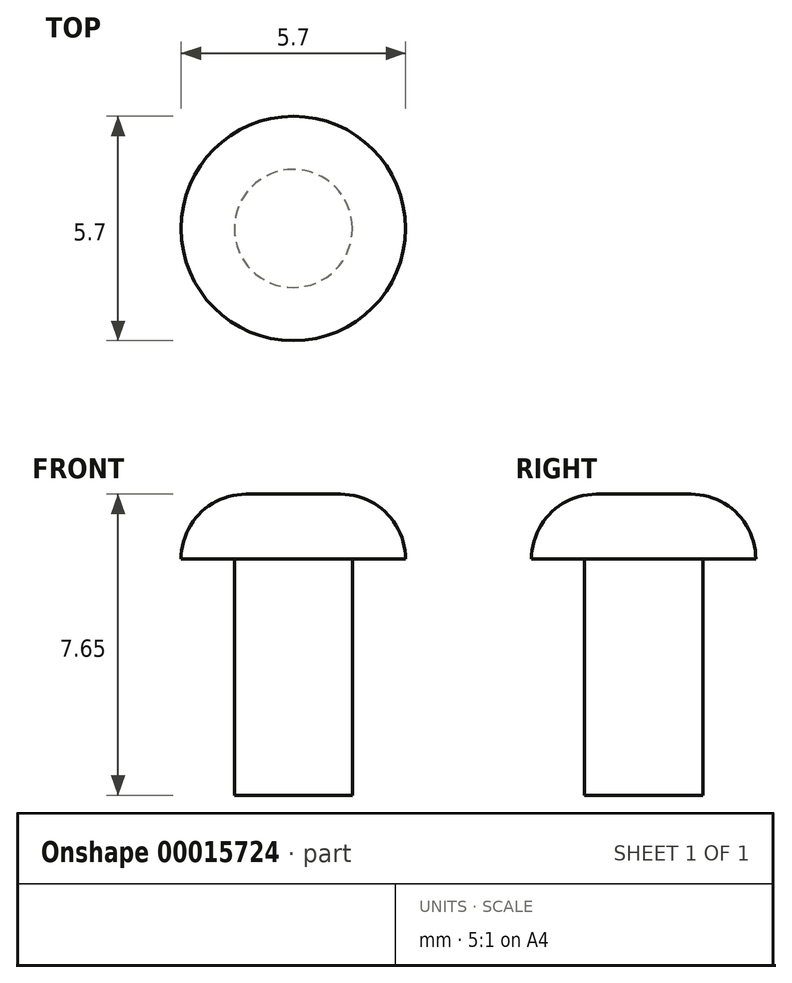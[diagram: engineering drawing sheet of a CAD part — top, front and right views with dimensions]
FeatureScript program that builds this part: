
annotation { "Feature Type Name" : "Feature", "Feature Type Description" : "" }
export const myFeature = defineFeature(function(context is Context, id is Id, definition is map)
    precondition{}
    {
        {
            var Q0;
            Q0=qCreatedBy(makeId("Top.planeOp"),FACE);
            var sketch = newSketch(context, id + "F0", { "sketchPlane" : qUnion([Q0])});
            skCircle(sketch, "E0", {"center": v(0, 0) * mm, "radius": 1.5 * mm});
            skSolve(sketch);
        }
        {
            var Q0;
            Q0 = qSketchRegion(id + "F0", true);
            extrude(context, id + "F1", {"entities" : qUnion([Q0]), "depth" : 6 * mm});
        }
        {
            var Q0;
            Q0=makeQuery(id+"F1.opExtrude","CAP_FACE",FACE,{"disambiguationData":[OSD([sQuery(id+"F0.wireOp",EDGE,"E0")])],"isStart":false});
            var sketch = newSketch(context, id + "F2", { "sketchPlane" : qUnion([Q0])});
            skCircle(sketch, "E1", {"center": v(0, 0) * mm, "radius": 2.85 * mm});
            skSolve(sketch);
        }
        {
            var Q0;
            Q0 = qSketchRegion(id + "F2", true);
            extrude(context, id + "F3", {"entities" : qUnion([Q0]), "operationType" : NewBodyOperationType.ADD, "depth" : 1.65 * mm});
        }
        {
            var Q0;
            Q0=makeQuery(id+"F3.opExtrude","CAP_EDGE",EDGE,{"disambiguationData":[OSD([sQuery(id+"F2.wireOp",EDGE,"E1")])],"isStart":false});
            fillet(context, id + "F4", {"entities" : qUnion([Q0]), "radius" : 1.65 * mm, "tangentPropagation" : true, "allowEdgeOverflow" : false});
        }
    });
